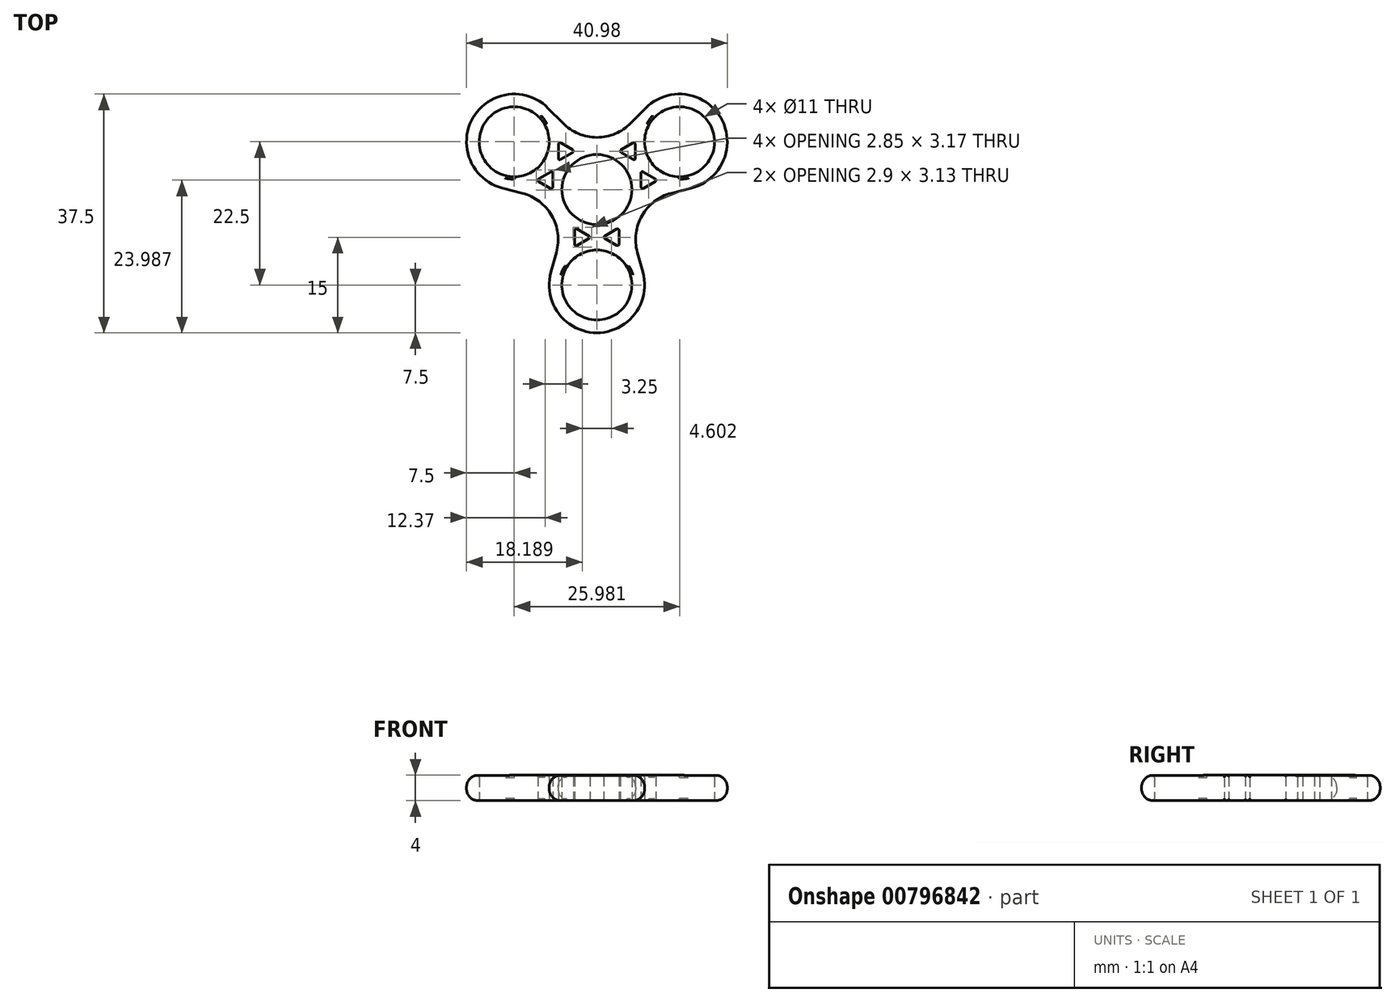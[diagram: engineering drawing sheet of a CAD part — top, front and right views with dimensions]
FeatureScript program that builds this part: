
annotation { "Feature Type Name" : "Feature", "Feature Type Description" : "" }
export const myFeature = defineFeature(function(context is Context, id is Id, definition is map)
    precondition{}
    {
        {
            var Q0;
            Q0=qCreatedBy(makeId("Top.planeOp"),FACE);
            var sketch = newSketch(context, id + "F0", { "sketchPlane" : qUnion([Q0])});
            skLineSegment(sketch, "E0", {"start": v(0, 0) * mm, "end": v(-13, 7.5) * mm, "construction": true});
            skLineSegment(sketch, "E1", {"start": v(0, 0) * mm, "end": v(0, -15) * mm, "construction": true});
            skLineSegment(sketch, "E2", {"start": v(0, 0) * mm, "end": v(13, 7.5) * mm, "construction": true});
            skCircle(sketch, "E3", {"center": v(-13, 7.5) * mm, "radius": 5.5 * mm});
            skCircle(sketch, "E4", {"center": v(13, 7.5) * mm, "radius": 5.5 * mm});
            skCircle(sketch, "E5", {"center": v(0, -15) * mm, "radius": 5.5 * mm});
            skArc(sketch, "E6", {"start": v(-7.65, 12.76) * mm, "mid": v(-19.49, 11.25) * mm, "end": v(-14.88, 0.24) * mm});
            skArc(sketch, "E7", {"start": v(-7.23, -13) * mm, "mid": v(0, -22.5) * mm, "end": v(7.23, -13) * mm});
            skArc(sketch, "E8", {"start": v(14.88, 0.24) * mm, "mid": v(19.49, 11.25) * mm, "end": v(7.65, 12.76) * mm});
            skLineSegment(sketch, "E9", {"start": v(-7.65, 12.76) * mm, "end": v(-5.34, 10.42) * mm});
            skLineSegment(sketch, "E10", {"start": v(5.34, 10.42) * mm, "end": v(7.65, 12.76) * mm});
            skPoint(sketch, "E11.visualSharp", {"position": v(0, 5) * mm});
            skArc(sketch, "E11.filletArc", {"start": v(-5.34, 10.42) * mm, "mid": v(0, 8.19) * mm, "end": v(5.34, 10.42) * mm});
            skLineSegment(sketch, "E12", {"start": v(0, 0) * mm, "end": v(13, -7.5) * mm, "construction": true});
            skLineSegment(sketch, "E13", {"start": v(7.23, -13) * mm, "end": v(6.36, -9.84) * mm});
            skLineSegment(sketch, "E14", {"start": v(11.7, -0.58) * mm, "end": v(14.88, 0.24) * mm});
            skPoint(sketch, "E15.visualSharp", {"position": v(4.33, -2.5) * mm});
            skArc(sketch, "E15.filletArc", {"start": v(11.7, -0.58) * mm, "mid": v(7.1, -4.1) * mm, "end": v(6.36, -9.84) * mm});
            skLineSegment(sketch, "E16", {"start": v(0, 0) * mm, "end": v(-13, -7.5) * mm, "construction": true});
            skLineSegment(sketch, "E17", {"start": v(-11.7, -0.58) * mm, "end": v(-14.88, 0.24) * mm});
            skLineSegment(sketch, "E18", {"start": v(-6.36, -9.84) * mm, "end": v(-7.23, -13) * mm});
            skPoint(sketch, "E19.visualSharp", {"position": v(-4.33, -2.5) * mm});
            skArc(sketch, "E19.filletArc", {"start": v(-6.36, -9.84) * mm, "mid": v(-7.1, -4.1) * mm, "end": v(-11.7, -0.58) * mm});
            skCircle(sketch, "E20", {"center": v(0, 0) * mm, "radius": 5.5 * mm});
            skSolve(sketch);
        }
        {
            var Q0;
            Q0=makeQuery(id+"F0.imprint","IMPRINT",FACE,{"disambiguationData":[TD([[makeQuery(id+"F0.imprint","IMPRINT",EDGE,{"derivedFrom":sQuery(id+"F0.wireOp",EDGE,"E3")}),-1.0]])]});
            extrude(context, id + "F1", {"entities" : qUnion([Q0]), "depth" : 4 * mm, "offsetDistance" : 25 * mm});
        }
        {
            var Q0;
            Q0=makeQuery(id+"F1.opExtrude","SWEPT_FACE",FACE,{"disambiguationData":[OSD([sQuery(id+"F0.wireOp",EDGE,"E15.filletArc")])]});
            var Q1;
            Q1=makeQuery(id+"F1.opExtrude","SWEPT_FACE",FACE,{"disambiguationData":[OSD([sQuery(id+"F0.wireOp",EDGE,"E7")])]});
            var Q2;
            Q2=makeQuery(id+"F1.opExtrude","SWEPT_FACE",FACE,{"disambiguationData":[OSD([sQuery(id+"F0.wireOp",EDGE,"E13")])]});
            var Q3;
            Q3=makeQuery(id+"F1.opExtrude","SWEPT_FACE",FACE,{"disambiguationData":[OSD([sQuery(id+"F0.wireOp",EDGE,"E8")])]});
            var Q4;
            Q4=makeQuery(id+"F1.opExtrude","SWEPT_FACE",FACE,{"disambiguationData":[OSD([sQuery(id+"F0.wireOp",EDGE,"E14")])]});
            var Q5;
            Q5=makeQuery(id+"F1.opExtrude","SWEPT_FACE",FACE,{"disambiguationData":[OSD([sQuery(id+"F0.wireOp",EDGE,"E19.filletArc")])]});
            var Q6;
            Q6=makeQuery(id+"F1.opExtrude","SWEPT_FACE",FACE,{"disambiguationData":[OSD([sQuery(id+"F0.wireOp",EDGE,"E18")])]});
            var Q7;
            Q7=makeQuery(id+"F1.opExtrude","SWEPT_FACE",FACE,{"disambiguationData":[OSD([sQuery(id+"F0.wireOp",EDGE,"E6")])]});
            var Q8;
            Q8=makeQuery(id+"F1.opExtrude","SWEPT_FACE",FACE,{"disambiguationData":[OSD([sQuery(id+"F0.wireOp",EDGE,"E17")])]});
            var Q9;
            Q9=makeQuery(id+"F1.opExtrude","SWEPT_FACE",FACE,{"disambiguationData":[OSD([sQuery(id+"F0.wireOp",EDGE,"E9")])]});
            var Q10;
            Q10=makeQuery(id+"F1.opExtrude","SWEPT_FACE",FACE,{"disambiguationData":[OSD([sQuery(id+"F0.wireOp",EDGE,"E11.filletArc")])]});
            var Q11;
            Q11=makeQuery(id+"F1.opExtrude","SWEPT_FACE",FACE,{"disambiguationData":[OSD([sQuery(id+"F0.wireOp",EDGE,"E10")])]});
            fillet(context, id + "F2", {"entities" : qUnion([Q0, Q1, Q2, Q3, Q4, Q5, Q6, Q7, Q8, Q9, Q10, Q11]), "radius" : 1.85 * mm, "tangentPropagation" : true, "allowEdgeOverflow" : false});
        }
        {
            var Q0;
            Q0=makeQuery(id+"F1.opExtrude","SWEPT_FACE",FACE,{"disambiguationData":[OSD([sQuery(id+"F0.wireOp",EDGE,"E20")])]});
            var Q1;
            Q1=makeQuery(id+"F1.opExtrude","SWEPT_FACE",FACE,{"disambiguationData":[OSD([sQuery(id+"F0.wireOp",EDGE,"E5")])]});
            var Q2;
            Q2=makeQuery(id+"F1.opExtrude","SWEPT_FACE",FACE,{"disambiguationData":[OSD([sQuery(id+"F0.wireOp",EDGE,"E4")])]});
            var Q3;
            Q3=makeQuery(id+"F1.opExtrude","SWEPT_FACE",FACE,{"disambiguationData":[OSD([sQuery(id+"F0.wireOp",EDGE,"E3")])]});
            fillet(context, id + "F3", {"entities" : qUnion([Q0, Q1, Q2, Q3]), "radius" : .35 * mm, "tangentPropagation" : true, "allowEdgeOverflow" : false});
        }
        {
            var Q0;
            Q0=makeQuery(id+"F1.opExtrude","CAP_FACE",FACE,{"disambiguationData":[OSD([sQuery(id+"F0.wireOp",EDGE,"E3"),sQuery(id+"F0.wireOp",EDGE,"E4"),sQuery(id+"F0.wireOp",EDGE,"E5"),sQuery(id+"F0.wireOp",EDGE,"E6"),sQuery(id+"F0.wireOp",EDGE,"E7"),sQuery(id+"F0.wireOp",EDGE,"E8"),sQuery(id+"F0.wireOp",EDGE,"E9"),sQuery(id+"F0.wireOp",EDGE,"E10"),sQuery(id+"F0.wireOp",EDGE,"E11.filletArc"),sQuery(id+"F0.wireOp",EDGE,"E13"),sQuery(id+"F0.wireOp",EDGE,"E14"),sQuery(id+"F0.wireOp",EDGE,"E15.filletArc"),sQuery(id+"F0.wireOp",EDGE,"E17"),sQuery(id+"F0.wireOp",EDGE,"E18"),sQuery(id+"F0.wireOp",EDGE,"E19.filletArc"),sQuery(id+"F0.wireOp",EDGE,"E20")])],"isStart":true});
            var sketch = newSketch(context, id + "F4", { "sketchPlane" : qUnion([Q0])});
            skLineSegment(sketch, "E21", {"start": v(-3.5, 8.57) * mm, "end": v(-3.5, 6.43) * mm});
            skLineSegment(sketch, "E22", {"start": v(-3.13, 6.22) * mm, "end": v(-1.2, 7.33) * mm});
            skLineSegment(sketch, "E23", {"start": v(1.2, 7.33) * mm, "end": v(3.12, 6.22) * mm});
            skLineSegment(sketch, "E24", {"start": v(3.5, 6.43) * mm, "end": v(3.5, 8.57) * mm});
            skLineSegment(sketch, "E25", {"start": v(3.12, 8.78) * mm, "end": v(1.2, 7.67) * mm});
            skLineSegment(sketch, "E26", {"start": v(-1.2, 7.67) * mm, "end": v(-3.13, 8.78) * mm});
            skPoint(sketch, "E27.visualSharp", {"position": v(-3.5, 9) * mm});
            skArc(sketch, "E27.filletArc", {"start": v(-3.13, 8.78) * mm, "mid": v(-3.38, 8.78) * mm, "end": v(-3.5, 8.57) * mm});
            skPoint(sketch, "E28.visualSharp", {"position": v(-3.5, 6) * mm});
            skArc(sketch, "E28.filletArc", {"start": v(-3.5, 6.43) * mm, "mid": v(-3.38, 6.22) * mm, "end": v(-3.13, 6.22) * mm});
            skPoint(sketch, "E29.visualSharp", {"position": v(3.5, 6) * mm});
            skArc(sketch, "E29.filletArc", {"start": v(3.12, 6.22) * mm, "mid": v(3.37, 6.22) * mm, "end": v(3.5, 6.43) * mm});
            skPoint(sketch, "E30.visualSharp", {"position": v(3.5, 9) * mm});
            skArc(sketch, "E30.filletArc", {"start": v(3.5, 8.57) * mm, "mid": v(3.37, 8.78) * mm, "end": v(3.12, 8.78) * mm});
            skPoint(sketch, "E31.visualSharp", {"position": v(0, 8.02) * mm});
            skPoint(sketch, "E32.visualSharp", {"position": v(0, 6.98) * mm});
            skArc(sketch, "E33.filletArc", {"start": v(-1.2, 7.33) * mm, "mid": v(-1.1, 7.5) * mm, "end": v(-1.2, 7.67) * mm});
            skArc(sketch, "E34.filletArc", {"start": v(1.2, 7.67) * mm, "mid": v(1.1, 7.5) * mm, "end": v(1.2, 7.33) * mm});
            skPoint(sketch, "E35.centerSnap0", {"position": v(-1.1, 7.5) * mm});
            skPoint(sketch, "E36.centerSnap0", {"position": v(1.1, 7.5) * mm});
            skLineSegment(sketch, "E37.1.0", {"start": v(-7.32, -0.19) * mm, "end": v(-9.17, -1.25) * mm});
            skPoint(sketch, "E37.1.1", {"position": v(-6.95, 0.03) * mm});
            skLineSegment(sketch, "E37.1.2", {"start": v(-3.82, -5.81) * mm, "end": v(-5.74, -4.7) * mm});
            skArc(sketch, "E37.1.3", {"start": v(-9.17, -1.25) * mm, "mid": v(-9.3, -1.47) * mm, "end": v(-9.17, -1.69) * mm});
            skLineSegment(sketch, "E37.1.4", {"start": v(-9.17, -1.69) * mm, "end": v(-7.25, -2.8) * mm});
            skArc(sketch, "E37.1.5", {"start": v(-3.82, -6.25) * mm, "mid": v(-3.7, -6.03) * mm, "end": v(-3.82, -5.81) * mm});
            skArc(sketch, "E37.1.6", {"start": v(-6.04, -7.1) * mm, "mid": v(-5.92, -7.31) * mm, "end": v(-5.67, -7.31) * mm});
            skPoint(sketch, "E37.1.7", {"position": v(-6.04, -7.53) * mm});
            skPoint(sketch, "E37.1.8", {"position": v(-6.95, -4.01) * mm});
            skLineSegment(sketch, "E37.1.9", {"start": v(-6.04, -4.88) * mm, "end": v(-6.04, -7.1) * mm});
            skPoint(sketch, "E37.1.10", {"position": v(-3.45, -6.03) * mm});
            skPoint(sketch, "E37.1.11", {"position": v(-5.94, -4.7) * mm});
            skPoint(sketch, "E37.1.12", {"position": v(-9.54, -1.47) * mm});
            skLineSegment(sketch, "E37.1.13", {"start": v(-5.67, -7.31) * mm, "end": v(-3.82, -6.25) * mm});
            skArc(sketch, "E37.1.14", {"start": v(-6.95, -0.4) * mm, "mid": v(-7.07, -0.19) * mm, "end": v(-7.32, -0.19) * mm});
            skPoint(sketch, "E37.1.15", {"position": v(-7.05, -2.8) * mm});
            skLineSegment(sketch, "E37.1.16", {"start": v(-6.95, -2.62) * mm, "end": v(-6.95, -0.4) * mm});
            skPoint(sketch, "E37.1.17", {"position": v(-6.04, -3.49) * mm});
            skArc(sketch, "E37.1.18", {"start": v(-7.25, -2.8) * mm, "mid": v(-7.05, -2.8) * mm, "end": v(-6.95, -2.62) * mm});
            skArc(sketch, "E37.1.19", {"start": v(-5.74, -4.7) * mm, "mid": v(-5.94, -4.7) * mm, "end": v(-6.04, -4.88) * mm});
            skLineSegment(sketch, "E37.2.0", {"start": v(3.82, -6.25) * mm, "end": v(5.67, -7.31) * mm});
            skPoint(sketch, "E37.2.1", {"position": v(3.45, -6.03) * mm});
            skLineSegment(sketch, "E37.2.2", {"start": v(6.95, -0.4) * mm, "end": v(6.95, -2.62) * mm});
            skArc(sketch, "E37.2.3", {"start": v(5.67, -7.31) * mm, "mid": v(5.92, -7.31) * mm, "end": v(6.04, -7.1) * mm});
            skLineSegment(sketch, "E37.2.4", {"start": v(6.04, -7.1) * mm, "end": v(6.04, -4.88) * mm});
            skArc(sketch, "E37.2.5", {"start": v(7.32, -0.19) * mm, "mid": v(7.07, -0.19) * mm, "end": v(6.95, -0.4) * mm});
            skArc(sketch, "E37.2.6", {"start": v(9.17, -1.69) * mm, "mid": v(9.3, -1.47) * mm, "end": v(9.17, -1.25) * mm});
            skPoint(sketch, "E37.2.7", {"position": v(9.54, -1.47) * mm});
            skPoint(sketch, "E37.2.8", {"position": v(6.95, -4.01) * mm});
            skLineSegment(sketch, "E37.2.9", {"start": v(7.25, -2.8) * mm, "end": v(9.17, -1.69) * mm});
            skPoint(sketch, "E37.2.10", {"position": v(6.95, 0.03) * mm});
            skPoint(sketch, "E37.2.11", {"position": v(7.05, -2.8) * mm});
            skPoint(sketch, "E37.2.12", {"position": v(6.04, -7.53) * mm});
            skLineSegment(sketch, "E37.2.13", {"start": v(9.17, -1.25) * mm, "end": v(7.32, -0.19) * mm});
            skArc(sketch, "E37.2.14", {"start": v(3.82, -5.81) * mm, "mid": v(3.7, -6.03) * mm, "end": v(3.82, -6.25) * mm});
            skPoint(sketch, "E37.2.15", {"position": v(5.94, -4.7) * mm});
            skLineSegment(sketch, "E37.2.16", {"start": v(5.74, -4.7) * mm, "end": v(3.82, -5.81) * mm});
            skPoint(sketch, "E37.2.17", {"position": v(6.04, -3.49) * mm});
            skArc(sketch, "E37.2.18", {"start": v(6.04, -4.88) * mm, "mid": v(5.94, -4.7) * mm, "end": v(5.74, -4.7) * mm});
            skArc(sketch, "E37.2.19", {"start": v(6.95, -2.62) * mm, "mid": v(7.05, -2.8) * mm, "end": v(7.25, -2.8) * mm});
            skPoint(sketch, "E37.center", {"position": v(0, 0) * mm});
            skSolve(sketch);
        }
        {
            var Q0;
            Q0=makeQuery(id+"F4.imprint","IMPRINT",FACE,{"disambiguationData":[TD([[makeQuery(id+"F4.imprint","IMPRINT",EDGE,{"derivedFrom":sQuery(id+"F4.wireOp",EDGE,"E21")}),1.0]])]});
            var Q1;
            Q1=makeQuery(id+"F4.imprint","IMPRINT",FACE,{"disambiguationData":[TD([[makeQuery(id+"F4.imprint","IMPRINT",EDGE,{"derivedFrom":sQuery(id+"F4.wireOp",EDGE,"a42ef246-e60e-49e6-ac22-d768403973c1.1.2")}),1.0]])]});
            var Q2;
            Q2=makeQuery(id+"F4.imprint","IMPRINT",FACE,{"disambiguationData":[TD([[makeQuery(id+"F4.imprint","IMPRINT",EDGE,{"derivedFrom":sQuery(id+"F4.wireOp",EDGE,"a42ef246-e60e-49e6-ac22-d768403973c1.2.2")}),1.0]])]});
            var Q3;
            Q3=makeQuery(id+"F4.imprint","IMPRINT",FACE,{"disambiguationData":[TD([[makeQuery(id+"F4.imprint","IMPRINT",EDGE,{"derivedFrom":sQuery(id+"F4.wireOp",EDGE,"E35")}),1.0]])]});
            var Q4;
            Q4=makeQuery(id+"F4.imprint","IMPRINT",FACE,{"disambiguationData":[TD([[makeQuery(id+"F4.imprint","IMPRINT",EDGE,{"derivedFrom":sQuery(id+"F4.wireOp",EDGE,"E23")}),1.0]])]});
            var Q5;
            Q5=makeQuery(id+"F4.imprint","IMPRINT",FACE,{"disambiguationData":[TD([[makeQuery(id+"F4.imprint","IMPRINT",EDGE,{"derivedFrom":sQuery(id+"F4.wireOp",EDGE,"E36")}),1.0]])]});
            var Q6;
            Q6=makeQuery(id+"F4.imprint","IMPRINT",FACE,{"disambiguationData":[TD([[makeQuery(id+"F4.imprint","IMPRINT",EDGE,{"derivedFrom":sQuery(id+"F4.wireOp",EDGE,"E37.2.2")}),1.0]])]});
            var Q7;
            Q7=makeQuery(id+"F4.imprint","IMPRINT",FACE,{"disambiguationData":[TD([[makeQuery(id+"F4.imprint","IMPRINT",EDGE,{"derivedFrom":sQuery(id+"F4.wireOp",EDGE,"E37.2.0")}),1.0]])]});
            var Q8;
            Q8=makeQuery(id+"F4.imprint","IMPRINT",FACE,{"disambiguationData":[TD([[makeQuery(id+"F4.imprint","IMPRINT",EDGE,{"derivedFrom":sQuery(id+"F4.wireOp",EDGE,"E37.1.2")}),1.0]])]});
            var Q9;
            Q9=makeQuery(id+"F4.imprint","IMPRINT",FACE,{"disambiguationData":[TD([[makeQuery(id+"F4.imprint","IMPRINT",EDGE,{"derivedFrom":sQuery(id+"F4.wireOp",EDGE,"E37.1.0")}),1.0]])]});
            extrude(context, id + "F5", {"entities" : qUnion([Q0, Q1, Q2, Q3, Q4, Q5, Q6, Q7, Q8, Q9]), "operationType" : NewBodyOperationType.REMOVE, "endBound" : BoundingType.UP_TO_NEXT, "oppositeDirection" : true, "depth" : 25 * mm, "offsetDistance" : 25 * mm});
        }
        {
            var Q0;
            Q0=makeQuery(id+"F5.boolean.opBoolean","COPY",FACE,{"derivedFrom":makeQuery(id+"F5.opExtrude","SWEPT_FACE",FACE,{"disambiguationData":[OSD([sQuery(id+"F4.wireOp",EDGE,"E23")])]})});
            var Q1;
            Q1=makeQuery(id+"F5.boolean.opBoolean","COPY",FACE,{"derivedFrom":makeQuery(id+"F5.opExtrude","SWEPT_FACE",FACE,{"disambiguationData":[OSD([sQuery(id+"F4.wireOp",EDGE,"E31.filletArc")])]})});
            var Q2;
            Q2=makeQuery(id+"F5.boolean.opBoolean","COPY",FACE,{"derivedFrom":makeQuery(id+"F5.opExtrude","SWEPT_FACE",FACE,{"disambiguationData":[OSD([sQuery(id+"F4.wireOp",EDGE,"E22")])]})});
            var Q3;
            Q3=makeQuery(id+"F5.boolean.opBoolean","COPY",FACE,{"derivedFrom":makeQuery(id+"F5.opExtrude","SWEPT_FACE",FACE,{"disambiguationData":[OSD([sQuery(id+"F4.wireOp",EDGE,"E28.filletArc")])]})});
            var Q4;
            Q4=makeQuery(id+"F5.boolean.opBoolean","COPY",FACE,{"derivedFrom":makeQuery(id+"F5.opExtrude","SWEPT_FACE",FACE,{"disambiguationData":[OSD([sQuery(id+"F4.wireOp",EDGE,"E21")])]})});
            var Q5;
            Q5=makeQuery(id+"F5.boolean.opBoolean","COPY",FACE,{"derivedFrom":makeQuery(id+"F5.opExtrude","SWEPT_FACE",FACE,{"disambiguationData":[OSD([sQuery(id+"F4.wireOp",EDGE,"E27.filletArc")])]})});
            var Q6;
            Q6=makeQuery(id+"F5.boolean.opBoolean","COPY",FACE,{"derivedFrom":makeQuery(id+"F5.opExtrude","SWEPT_FACE",FACE,{"disambiguationData":[OSD([sQuery(id+"F4.wireOp",EDGE,"E26")])]})});
            var Q7;
            Q7=makeQuery(id+"F5.boolean.opBoolean","COPY",FACE,{"derivedFrom":makeQuery(id+"F5.opExtrude","SWEPT_FACE",FACE,{"disambiguationData":[OSD([sQuery(id+"F4.wireOp",EDGE,"E25")])]})});
            var Q8;
            Q8=makeQuery(id+"F5.boolean.opBoolean","COPY",FACE,{"derivedFrom":makeQuery(id+"F5.opExtrude","SWEPT_FACE",FACE,{"disambiguationData":[OSD([sQuery(id+"F4.wireOp",EDGE,"E32.filletArc")])]})});
            var Q9;
            Q9=makeQuery(id+"F5.boolean.opBoolean","COPY",FACE,{"derivedFrom":makeQuery(id+"F5.opExtrude","SWEPT_FACE",FACE,{"disambiguationData":[OSD([sQuery(id+"F4.wireOp",EDGE,"E24")])]})});
            var Q10;
            Q10=makeQuery(id+"F5.boolean.opBoolean","COPY",FACE,{"derivedFrom":makeQuery(id+"F5.opExtrude","SWEPT_FACE",FACE,{"disambiguationData":[OSD([sQuery(id+"F4.wireOp",EDGE,"E30.filletArc")])]})});
            var Q11;
            Q11=makeQuery(id+"F5.boolean.opBoolean","COPY",FACE,{"derivedFrom":makeQuery(id+"F5.opExtrude","SWEPT_FACE",FACE,{"disambiguationData":[OSD([sQuery(id+"F4.wireOp",EDGE,"E29.filletArc")])]})});
            var Q12;
            Q12=makeQuery(id+"F5.boolean.opBoolean","COPY",FACE,{"derivedFrom":makeQuery(id+"F5.opExtrude","SWEPT_FACE",FACE,{"disambiguationData":[OSD([sQuery(id+"F4.wireOp",EDGE,"a42ef246-e60e-49e6-ac22-d768403973c1.2.2")])]})});
            var Q13;
            Q13=makeQuery(id+"F5.boolean.opBoolean","COPY",FACE,{"derivedFrom":makeQuery(id+"F5.opExtrude","SWEPT_FACE",FACE,{"disambiguationData":[OSD([sQuery(id+"F4.wireOp",EDGE,"a42ef246-e60e-49e6-ac22-d768403973c1.2.14")])]})});
            var Q14;
            Q14=makeQuery(id+"F5.boolean.opBoolean","COPY",FACE,{"derivedFrom":makeQuery(id+"F5.opExtrude","SWEPT_FACE",FACE,{"disambiguationData":[OSD([sQuery(id+"F4.wireOp",EDGE,"a42ef246-e60e-49e6-ac22-d768403973c1.2.13")])]})});
            var Q15;
            Q15=makeQuery(id+"F5.boolean.opBoolean","COPY",FACE,{"derivedFrom":makeQuery(id+"F5.opExtrude","SWEPT_FACE",FACE,{"disambiguationData":[OSD([sQuery(id+"F4.wireOp",EDGE,"a42ef246-e60e-49e6-ac22-d768403973c1.2.8")])]})});
            var Q16;
            Q16=makeQuery(id+"F5.boolean.opBoolean","COPY",FACE,{"derivedFrom":makeQuery(id+"F5.opExtrude","SWEPT_FACE",FACE,{"disambiguationData":[OSD([sQuery(id+"F4.wireOp",EDGE,"a42ef246-e60e-49e6-ac22-d768403973c1.2.7")])]})});
            var Q17;
            Q17=makeQuery(id+"F5.boolean.opBoolean","COPY",FACE,{"derivedFrom":makeQuery(id+"F5.opExtrude","SWEPT_FACE",FACE,{"disambiguationData":[OSD([sQuery(id+"F4.wireOp",EDGE,"a42ef246-e60e-49e6-ac22-d768403973c1.2.17")])]})});
            var Q18;
            Q18=makeQuery(id+"F5.boolean.opBoolean","COPY",FACE,{"derivedFrom":makeQuery(id+"F5.opExtrude","SWEPT_FACE",FACE,{"disambiguationData":[OSD([sQuery(id+"F4.wireOp",EDGE,"a42ef246-e60e-49e6-ac22-d768403973c1.2.6")])]})});
            var Q19;
            Q19=makeQuery(id+"F5.boolean.opBoolean","COPY",FACE,{"derivedFrom":makeQuery(id+"F5.opExtrude","SWEPT_FACE",FACE,{"disambiguationData":[OSD([sQuery(id+"F4.wireOp",EDGE,"a42ef246-e60e-49e6-ac22-d768403973c1.2.12")])]})});
            var Q20;
            Q20=makeQuery(id+"F5.boolean.opBoolean","COPY",FACE,{"derivedFrom":makeQuery(id+"F5.opExtrude","SWEPT_FACE",FACE,{"disambiguationData":[OSD([sQuery(id+"F4.wireOp",EDGE,"a42ef246-e60e-49e6-ac22-d768403973c1.2.3")])]})});
            var Q21;
            Q21=makeQuery(id+"F5.boolean.opBoolean","COPY",EDGE,{"derivedFrom":makeQuery(id+"F5.opExtrude","CAP_EDGE",EDGE,{"disambiguationData":[OSD([sQuery(id+"F4.wireOp",EDGE,"a42ef246-e60e-49e6-ac22-d768403973c1.2.17")])],"isStart":true})});
            var Q22;
            Q22=makeQuery(id+"F5.boolean.opBoolean","COPY",FACE,{"derivedFrom":makeQuery(id+"F5.opExtrude","SWEPT_FACE",FACE,{"disambiguationData":[OSD([sQuery(id+"F4.wireOp",EDGE,"a42ef246-e60e-49e6-ac22-d768403973c1.2.16")])]})});
            var Q23;
            Q23=makeQuery(id+"F5.boolean.opBoolean","COPY",FACE,{"derivedFrom":makeQuery(id+"F5.opExtrude","SWEPT_FACE",FACE,{"disambiguationData":[OSD([sQuery(id+"F4.wireOp",EDGE,"a42ef246-e60e-49e6-ac22-d768403973c1.2.11")])]})});
            var Q24;
            Q24=makeQuery(id+"F5.boolean.opBoolean","COPY",FACE,{"derivedFrom":makeQuery(id+"F5.opExtrude","SWEPT_FACE",FACE,{"disambiguationData":[OSD([sQuery(id+"F4.wireOp",EDGE,"a42ef246-e60e-49e6-ac22-d768403973c1.2.5")])]})});
            var Q25;
            Q25=makeQuery(id+"F5.boolean.opBoolean","COPY",FACE,{"derivedFrom":makeQuery(id+"F5.opExtrude","SWEPT_FACE",FACE,{"disambiguationData":[OSD([sQuery(id+"F4.wireOp",EDGE,"a42ef246-e60e-49e6-ac22-d768403973c1.1.5")])]})});
            var Q26;
            Q26=makeQuery(id+"F5.boolean.opBoolean","COPY",FACE,{"derivedFrom":makeQuery(id+"F5.opExtrude","SWEPT_FACE",FACE,{"disambiguationData":[OSD([sQuery(id+"F4.wireOp",EDGE,"a42ef246-e60e-49e6-ac22-d768403973c1.1.11")])]})});
            var Q27;
            Q27=makeQuery(id+"F5.boolean.opBoolean","COPY",FACE,{"derivedFrom":makeQuery(id+"F5.opExtrude","SWEPT_FACE",FACE,{"disambiguationData":[OSD([sQuery(id+"F4.wireOp",EDGE,"a42ef246-e60e-49e6-ac22-d768403973c1.1.3")])]})});
            var Q28;
            Q28=makeQuery(id+"F5.boolean.opBoolean","COPY",FACE,{"derivedFrom":makeQuery(id+"F5.opExtrude","SWEPT_FACE",FACE,{"disambiguationData":[OSD([sQuery(id+"F4.wireOp",EDGE,"a42ef246-e60e-49e6-ac22-d768403973c1.1.12")])]})});
            var Q29;
            Q29=makeQuery(id+"F5.boolean.opBoolean","COPY",FACE,{"derivedFrom":makeQuery(id+"F5.opExtrude","SWEPT_FACE",FACE,{"disambiguationData":[OSD([sQuery(id+"F4.wireOp",EDGE,"a42ef246-e60e-49e6-ac22-d768403973c1.1.6")])]})});
            var Q30;
            Q30=makeQuery(id+"F5.boolean.opBoolean","COPY",FACE,{"derivedFrom":makeQuery(id+"F5.opExtrude","SWEPT_FACE",FACE,{"disambiguationData":[OSD([sQuery(id+"F4.wireOp",EDGE,"a42ef246-e60e-49e6-ac22-d768403973c1.1.7")])]})});
            var Q31;
            Q31=makeQuery(id+"F5.boolean.opBoolean","COPY",FACE,{"derivedFrom":makeQuery(id+"F5.opExtrude","SWEPT_FACE",FACE,{"disambiguationData":[OSD([sQuery(id+"F4.wireOp",EDGE,"a42ef246-e60e-49e6-ac22-d768403973c1.1.17")])]})});
            var Q32;
            Q32=makeQuery(id+"F5.boolean.opBoolean","COPY",FACE,{"derivedFrom":makeQuery(id+"F5.opExtrude","SWEPT_FACE",FACE,{"disambiguationData":[OSD([sQuery(id+"F4.wireOp",EDGE,"a42ef246-e60e-49e6-ac22-d768403973c1.1.13")])]})});
            var Q33;
            Q33=makeQuery(id+"F5.boolean.opBoolean","COPY",FACE,{"derivedFrom":makeQuery(id+"F5.opExtrude","SWEPT_FACE",FACE,{"disambiguationData":[OSD([sQuery(id+"F4.wireOp",EDGE,"a42ef246-e60e-49e6-ac22-d768403973c1.1.8")])]})});
            var Q34;
            Q34=makeQuery(id+"F5.boolean.opBoolean","COPY",FACE,{"derivedFrom":makeQuery(id+"F5.opExtrude","SWEPT_FACE",FACE,{"disambiguationData":[OSD([sQuery(id+"F4.wireOp",EDGE,"a42ef246-e60e-49e6-ac22-d768403973c1.1.14")])]})});
            var Q35;
            Q35=makeQuery(id+"F5.boolean.opBoolean","COPY",FACE,{"derivedFrom":makeQuery(id+"F5.opExtrude","SWEPT_FACE",FACE,{"disambiguationData":[OSD([sQuery(id+"F4.wireOp",EDGE,"a42ef246-e60e-49e6-ac22-d768403973c1.1.2")])]})});
            var Q36;
            Q36=makeQuery(id+"F5.boolean.opBoolean","COPY",FACE,{"derivedFrom":makeQuery(id+"F5.opExtrude","SWEPT_FACE",FACE,{"disambiguationData":[OSD([sQuery(id+"F4.wireOp",EDGE,"a42ef246-e60e-49e6-ac22-d768403973c1.1.16")])]})});
            var Q37;
            Q37=makeQuery(id+"F5.boolean.opBoolean","COPY",FACE,{"derivedFrom":makeQuery(id+"F5.opExtrude","SWEPT_FACE",FACE,{"disambiguationData":[OSD([sQuery(id+"F4.wireOp",EDGE,"E36")])]})});
            var Q38;
            Q38=makeQuery(id+"F5.boolean.opBoolean","COPY",FACE,{"derivedFrom":makeQuery(id+"F5.opExtrude","SWEPT_FACE",FACE,{"disambiguationData":[OSD([sQuery(id+"F4.wireOp",EDGE,"E37.2.13")])]})});
            var Q39;
            Q39=makeQuery(id+"F5.boolean.opBoolean","COPY",FACE,{"derivedFrom":makeQuery(id+"F5.opExtrude","SWEPT_FACE",FACE,{"disambiguationData":[OSD([sQuery(id+"F4.wireOp",EDGE,"E37.2.16")])]})});
            var Q40;
            Q40=makeQuery(id+"F5.boolean.opBoolean","COPY",FACE,{"derivedFrom":makeQuery(id+"F5.opExtrude","SWEPT_FACE",FACE,{"disambiguationData":[OSD([sQuery(id+"F4.wireOp",EDGE,"E37.1.2")])]})});
            var Q41;
            Q41=makeQuery(id+"F5.boolean.opBoolean","COPY",FACE,{"derivedFrom":makeQuery(id+"F5.opExtrude","SWEPT_FACE",FACE,{"disambiguationData":[OSD([sQuery(id+"F4.wireOp",EDGE,"E37.1.16")])]})});
            fillet(context, id + "F6", {"entities" : qUnion([Q0, Q1, Q2, Q3, Q4, Q5, Q6, Q7, Q8, Q9, Q10, Q11, Q12, Q13, Q14, Q15, Q16, Q17, Q18, Q19, Q20, Q21, Q22, Q23, Q24, Q25, Q26, Q27, Q28, Q29, Q30, Q31, Q32, Q33, Q34, Q35, Q36, Q37, Q38, Q39, Q40, Q41]), "radius" : .25 * mm, "tangentPropagation" : true, "allowEdgeOverflow" : false});
        }
    });
